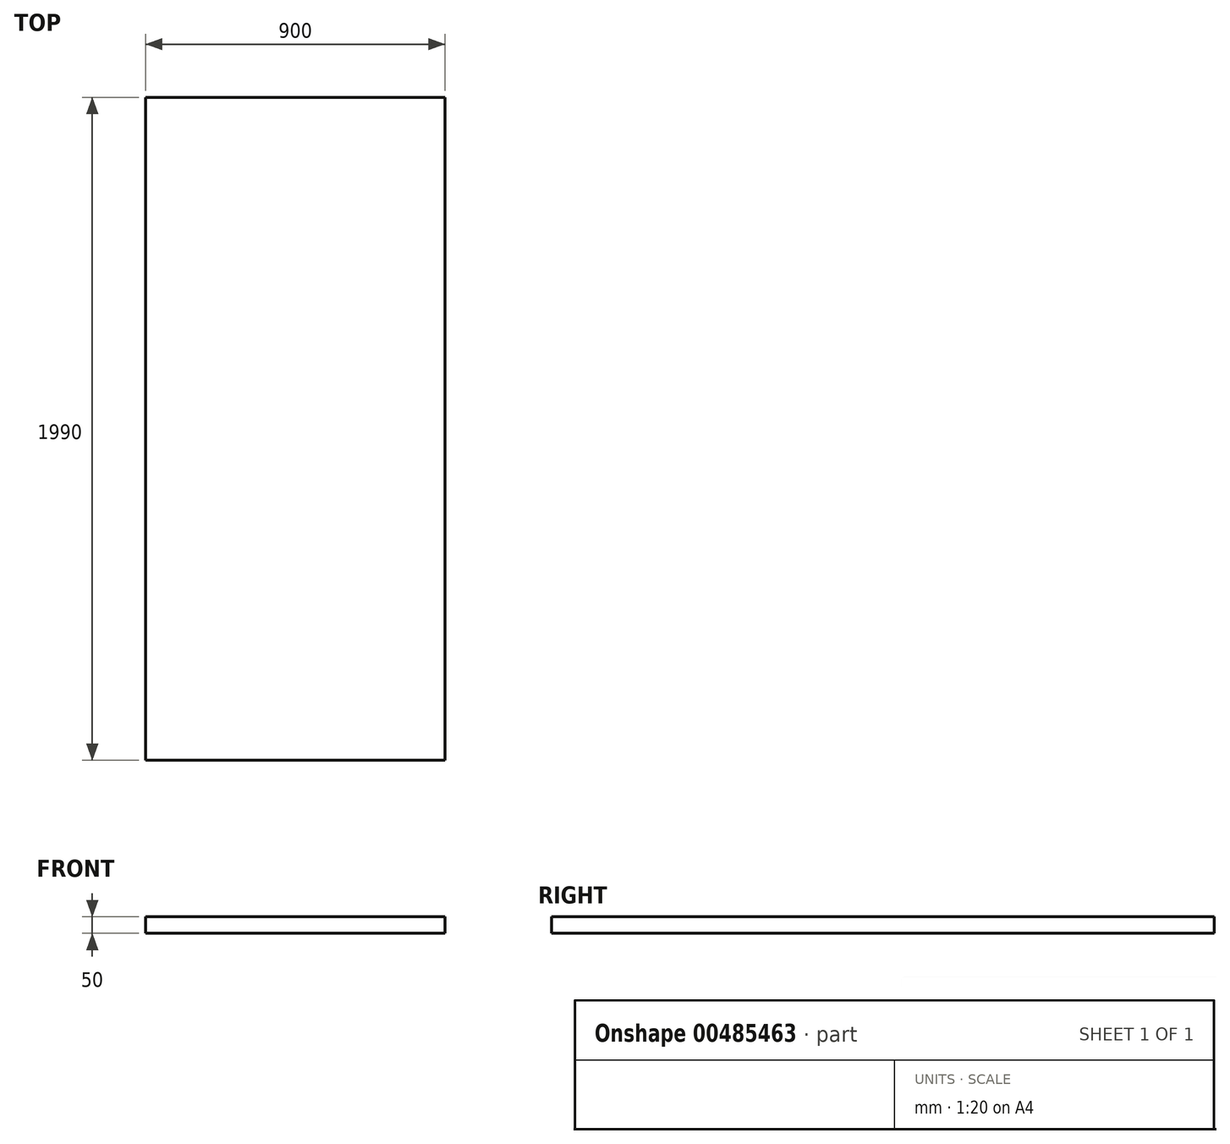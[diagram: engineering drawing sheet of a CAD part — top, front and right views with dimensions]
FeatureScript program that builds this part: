
annotation { "Feature Type Name" : "Feature", "Feature Type Description" : "" }
export const myFeature = defineFeature(function(context is Context, id is Id, definition is map)
    precondition{}
    {
        {
            var Q0;
            Q0=qCreatedBy(makeId("Top.planeOp"),FACE);
            var sketch = newSketch(context, id + "F0", { "sketchPlane" : qUnion([Q0])});
            skLineSegment(sketch, "E0.bottom", {"start": v(-525.8, 740.5) * mm, "end": v(374.2, 740.5) * mm});
            skLineSegment(sketch, "E0.top", {"start": v(-525.8, -1249.5) * mm, "end": v(374.2, -1249.5) * mm});
            skLineSegment(sketch, "E0.left", {"start": v(-525.8, 740.5) * mm, "end": v(-525.8, -1249.5) * mm});
            skLineSegment(sketch, "E0.right", {"start": v(374.2, 740.5) * mm, "end": v(374.2, -1249.5) * mm});
            skSolve(sketch);
        }
        {
            var Q0;
            Q0=qSketchRegion(id+"F0",true);
            extrude(context, id + "F1", {"entities" : qUnion([Q0]), "depth" : 50 * mm});
        }
    });
